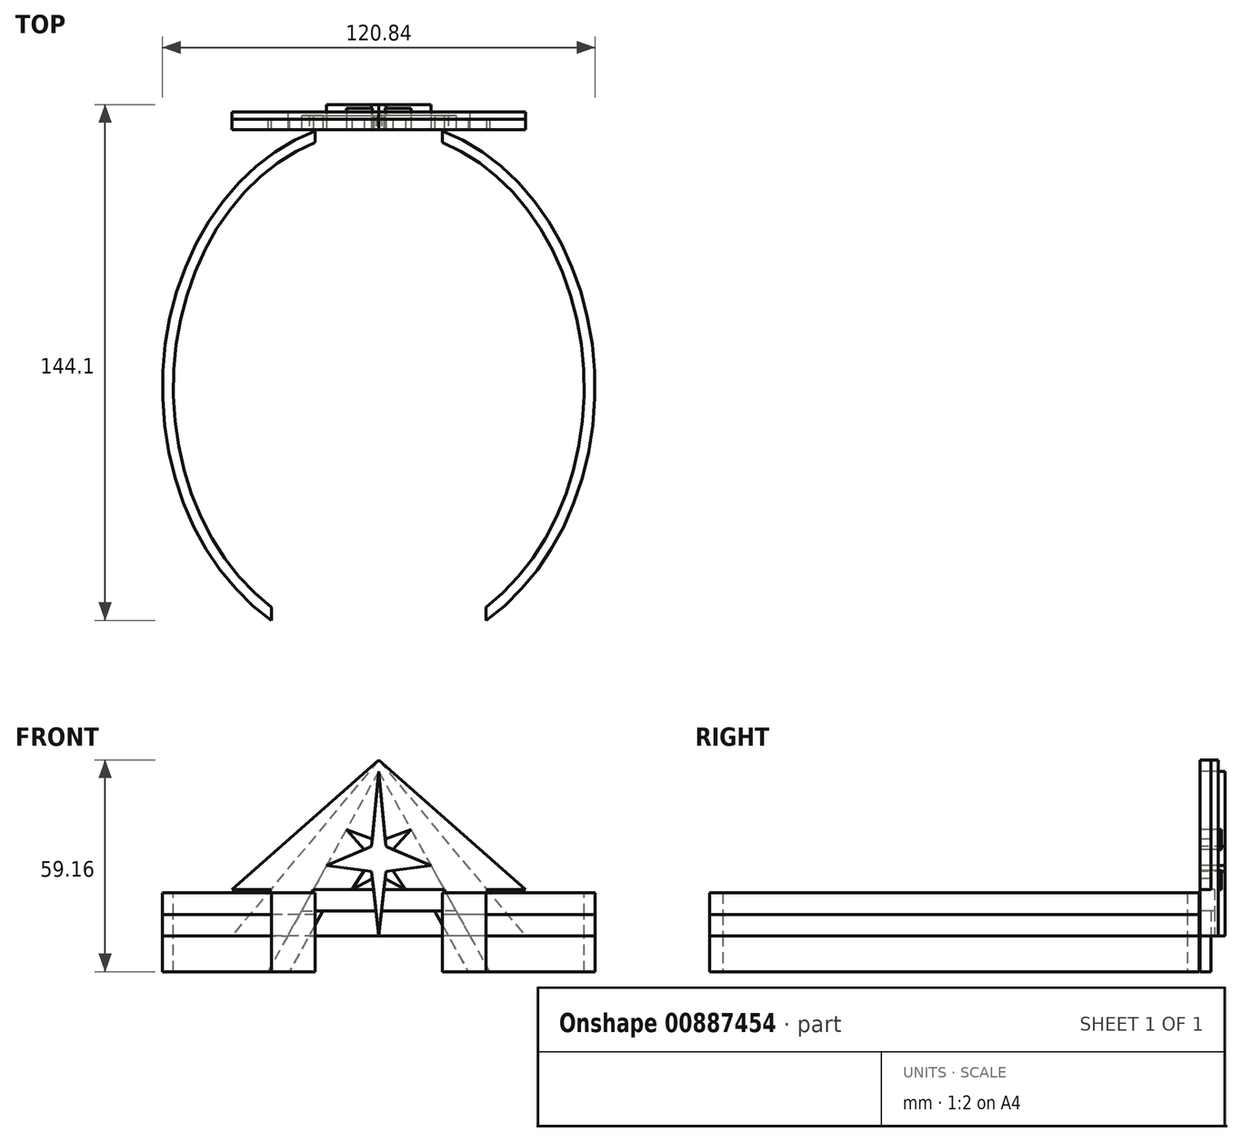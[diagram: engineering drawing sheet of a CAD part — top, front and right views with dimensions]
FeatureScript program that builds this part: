
annotation { "Feature Type Name" : "Feature", "Feature Type Description" : "" }
export const myFeature = defineFeature(function(context is Context, id is Id, definition is map)
    precondition{}
    {
        {
            var Q0;
            Q0=qCreatedBy(makeId("Top.planeOp"),FACE);
            var sketch = newSketch(context, id + "F0", { "sketchPlane" : qUnion([Q0])});
            skEllipse(sketch, "E0", {"center": v(0, 0) * mm, "majorRadius": 75 * mm, "minorRadius": 60.42 * mm, "majorAxis": v(0, 1)});
            skEllipse(sketch, "E1", {"center": v(0, 0) * mm, "majorRadius": 72 * mm, "minorRadius": 57.42 * mm, "majorAxis": v(0, 1)});
            skPoint(sketch, "E2", {"position": v(-60.42, 0) * mm});
            skPoint(sketch, "E3", {"position": v(-57.42, 0) * mm});
            skPoint(sketch, "E4", {"position": v(0, 7.93) * mm});
            skPoint(sketch, "E5", {"position": v(0, 72) * mm});
            skPoint(sketch, "E6", {"position": v(0, 75) * mm});
            skLineSegment(sketch, "E7.bottom", {"start": v(-30, 0) * mm, "end": v(30, 0) * mm});
            skLineSegment(sketch, "E7.top", {"start": v(-30, -85.78) * mm, "end": v(30, -85.78) * mm});
            skLineSegment(sketch, "E7.left", {"start": v(-30, 0) * mm, "end": v(-30, -85.78) * mm});
            skLineSegment(sketch, "E7.right", {"start": v(30, 0) * mm, "end": v(30, -85.78) * mm});
            skPoint(sketch, "E8", {"position": v(30, 0) * mm});
            skPoint(sketch, "E9", {"position": v(30, 74.8) * mm});
            skPoint(sketch, "E10", {"position": v(-30, 0) * mm});
            skPoint(sketch, "E11", {"position": v(-30, 74.8) * mm});
            skLineSegment(sketch, "E12.bottom", {"start": v(17.75, 57.73) * mm, "end": v(-17.75, 57.73) * mm});
            skLineSegment(sketch, "E12.top", {"start": v(17.75, 82.73) * mm, "end": v(-17.75, 82.73) * mm});
            skLineSegment(sketch, "E12.left", {"start": v(17.75, 57.73) * mm, "end": v(17.75, 82.73) * mm});
            skLineSegment(sketch, "E12.right", {"start": v(-17.75, 57.73) * mm, "end": v(-17.75, 82.73) * mm});
            skPoint(sketch, "E13", {"position": v(0, 57.73) * mm});
            skSolve(sketch);
        }
        {
            var Q0;
            {var subQ0=sQuery(id+"F0.wireOp",EDGE,"E7.left");var subQ1=sQuery(id+"F0.wireOp",EDGE,"E0");var subQ2=makeQuery(id+"F0.imprint","INTERSECT",VERTEX,{"derivedFrom":[subQ1,subQ0]});Q0=makeQuery(id+"F0.imprint","IMPRINT",FACE,{"disambiguationData":[TD([[makeQuery(id+"F0.imprint","IMPRINT",EDGE,{"disambiguationData":[TD([[subQ2,1.0]])],"derivedFrom":subQ1}),1.0]])]});}
            var Q1;
            {var subQ0=sQuery(id+"F0.wireOp",EDGE,"E7.right");var subQ1=sQuery(id+"F0.wireOp",EDGE,"E0");var subQ2=makeQuery(id+"F0.imprint","INTERSECT",VERTEX,{"derivedFrom":[subQ1,subQ0]});Q1=makeQuery(id+"F0.imprint","IMPRINT",FACE,{"disambiguationData":[TD([[makeQuery(id+"F0.imprint","IMPRINT",EDGE,{"disambiguationData":[TD([[subQ2,-1.0]])],"derivedFrom":subQ1}),1.0]])]});}
            extrude(context, id + "F1", {"entities" : qUnion([Q0, Q1]), "depth" : 10 * mm, "offsetDistance" : 25 * mm});
        }
        {
            var Q0;
            Q0=qCreatedBy(makeId("Top.planeOp"),FACE);
            cPlane(context, id + "F2", {"entities" : qUnion([Q0]), "cplaneType" : CPlaneType.OFFSET, "offset" : 10 * mm, "width" : 150 * mm, "height" : 150 * mm});
        }
        {
            var Q0;
            Q0=qCreatedBy(makeId("Top.planeOp"),FACE);
            cPlane(context, id + "F3", {"entities" : qUnion([Q0]), "cplaneType" : CPlaneType.OFFSET, "offset" : 16 * mm, "width" : 150 * mm, "height" : 150 * mm});
        }
        {
            var Q0;
            Q0=qCreatedBy(id+"F2.planeOp",FACE);
            var sketch = newSketch(context, id + "F4", { "sketchPlane" : qUnion([Q0])});
            skEllipse(sketch, "E14", {"center": v(0, 0) * mm, "majorRadius": 75 * mm, "minorRadius": 60.42 * mm, "majorAxis": v(0, 1)});
            skEllipse(sketch, "E15", {"center": v(0, 0) * mm, "majorRadius": 72 * mm, "minorRadius": 57.42 * mm, "majorAxis": v(0, 1)});
            skPoint(sketch, "E16", {"position": v(-60.42, 0) * mm});
            skPoint(sketch, "E17", {"position": v(-57.42, 0) * mm});
            skPoint(sketch, "E18", {"position": v(0, -14.53) * mm});
            skPoint(sketch, "E19", {"position": v(0, 72) * mm});
            skPoint(sketch, "E20", {"position": v(0, 75) * mm});
            skLineSegment(sketch, "E21.bottom", {"start": v(-30, 0) * mm, "end": v(30, 0) * mm});
            skLineSegment(sketch, "E21.top", {"start": v(-30, -85.78) * mm, "end": v(30, -85.78) * mm});
            skLineSegment(sketch, "E21.left", {"start": v(-30, 0) * mm, "end": v(-30, -85.78) * mm});
            skLineSegment(sketch, "E21.right", {"start": v(30, 0) * mm, "end": v(30, -85.78) * mm});
            skPoint(sketch, "E22", {"position": v(30, 0) * mm});
            skPoint(sketch, "E23", {"position": v(30, 52.33) * mm});
            skPoint(sketch, "E24", {"position": v(-30, 0) * mm});
            skPoint(sketch, "E25", {"position": v(-30, 52.33) * mm});
            skLineSegment(sketch, "E26.bottom", {"start": v(17.75, 57.73) * mm, "end": v(-17.75, 57.73) * mm});
            skLineSegment(sketch, "E26.top", {"start": v(17.75, 82.73) * mm, "end": v(-17.75, 82.73) * mm});
            skLineSegment(sketch, "E26.left", {"start": v(17.75, 57.73) * mm, "end": v(17.75, 82.73) * mm});
            skLineSegment(sketch, "E26.right", {"start": v(-17.75, 57.73) * mm, "end": v(-17.75, 82.73) * mm});
            skPoint(sketch, "E27", {"position": v(0, 57.73) * mm});
            skSolve(sketch);
        }
        {
            var Q0;
            Q0=qCreatedBy(makeId("Front.planeOp"),FACE);
            cPlane(context, id + "F5", {"entities" : qUnion([Q0]), "cplaneType" : CPlaneType.OFFSET, "offset" : 72 * mm, "oppositeDirection" : true, "width" : 150 * mm, "height" : 150 * mm});
        }
        {
            var Q0;
            Q0=qCreatedBy(id+"F5.planeOp",FACE);
            var sketch = newSketch(context, id + "F6", { "sketchPlane" : qUnion([Q0])});
            skPoint(sketch, "E28", {"position": v(0, 56) * mm});
            skLineSegment(sketch, "E29", {"start": v(0, 56) * mm, "end": v(30.98, 0) * mm});
            skPoint(sketch, "E30", {"position": v(40.98, 0) * mm});
            skPoint(sketch, "E31", {"position": v(40.98, 10) * mm});
            skPoint(sketch, "E32", {"position": v(0, 59.16) * mm});
            skLineSegment(sketch, "E33", {"start": v(0, 59.16) * mm, "end": v(40.98, 10) * mm});
            skPoint(sketch, "E34", {"position": v(40.98, 23) * mm});
            skLineSegment(sketch, "E35", {"start": v(0, 59.16) * mm, "end": v(40.98, 23) * mm});
            skPoint(sketch, "E36", {"position": v(30.15, 23) * mm});
            skPoint(sketch, "E37", {"position": v(40.98, 17) * mm});
            skPoint(sketch, "E38", {"position": v(21.58, 17) * mm});
            skPoint(sketch, "E39", {"position": v(18.26, 23) * mm});
            skLineSegment(sketch, "E40", {"start": v(18.26, 23) * mm, "end": v(0, 23) * mm});
            skLineSegment(sketch, "E41", {"start": v(21.58, 17) * mm, "end": v(0, 17) * mm});
            skPoint(sketch, "E42", {"position": v(0, 17) * mm});
            skPoint(sketch, "E43", {"position": v(0, 10) * mm});
            skPoint(sketch, "E44", {"position": v(24.98, 0) * mm});
            skPoint(sketch, "E45", {"position": v(15.58, 17) * mm});
            skLineSegment(sketch, "E46", {"start": v(15.58, 17) * mm, "end": v(24.98, 0) * mm});
            skPoint(sketch, "E47", {"position": v(25.45, 10) * mm});
            skLineSegment(sketch, "E48", {"start": v(19.45, 10) * mm, "end": v(0, 10) * mm});
            skLineSegment(sketch, "E49", {"start": v(40.98, 23) * mm, "end": v(30.15, 23) * mm});
            skPoint(sketch, "E50", {"position": v(0, 28) * mm});
            skPoint(sketch, "E51", {"position": v(0, 35) * mm});
            skPoint(sketch, "E52", {"position": v(2, 28) * mm});
            skPoint(sketch, "E53", {"position": v(2, 35) * mm});
            skLineSegment(sketch, "E54", {"start": v(0, 56) * mm, "end": v(2, 35) * mm});
            skLineSegment(sketch, "E55", {"start": v(2, 28) * mm, "end": v(2, 35) * mm});
            skLineSegment(sketch, "E56", {"start": v(2, 28) * mm, "end": v(0, 10) * mm});
            skPoint(sketch, "E57", {"position": v(14.56, 29.69) * mm});
            skLineSegment(sketch, "E58", {"start": v(2, 35) * mm, "end": v(14.56, 29.69) * mm});
            skLineSegment(sketch, "E59", {"start": v(2, 28) * mm, "end": v(14.56, 29.69) * mm});
            skPoint(sketch, "E60", {"position": v(9.02, 39.69) * mm});
            skPoint(sketch, "E61", {"position": v(4, 34.15) * mm});
            skPoint(sketch, "E62", {"position": v(1.81, 37) * mm});
            skLineSegment(sketch, "E63", {"start": v(9.02, 39.69) * mm, "end": v(4, 34.15) * mm});
            skLineSegment(sketch, "E64", {"start": v(9.02, 39.69) * mm, "end": v(1.81, 37) * mm});
            skPoint(sketch, "E65", {"position": v(7.44, 23) * mm});
            skPoint(sketch, "E66", {"position": v(1.44, 23) * mm});
            skPoint(sketch, "E67", {"position": v(4, 28.27) * mm});
            skLineSegment(sketch, "E68", {"start": v(4, 28.27) * mm, "end": v(7.44, 23) * mm});
            skPoint(sketch, "E69", {"position": v(1.78, 26) * mm});
            skLineSegment(sketch, "E70", {"start": v(1.78, 26) * mm, "end": v(7.44, 23) * mm});
            skLineSegment(sketch, "E71.MirrorCS", {"start": v(0, 56) * mm, "end": v(-2, 35) * mm});
            skLineSegment(sketch, "E72.MirrorCS", {"start": v(-9.02, 39.69) * mm, "end": v(-1.81, 37) * mm});
            skLineSegment(sketch, "E73.MirrorCS", {"start": v(0, 56) * mm, "end": v(-30.98, 0) * mm});
            skLineSegment(sketch, "E74.MirrorCS", {"start": v(-9.02, 39.69) * mm, "end": v(-4, 34.15) * mm});
            skLineSegment(sketch, "E75.MirrorCS", {"start": v(-2, 35) * mm, "end": v(-14.56, 29.69) * mm});
            skLineSegment(sketch, "E76.MirrorCS", {"start": v(-2, 28) * mm, "end": v(-14.56, 29.69) * mm});
            skLineSegment(sketch, "E77.MirrorCS", {"start": v(-4, 28.27) * mm, "end": v(-7.44, 23) * mm});
            skLineSegment(sketch, "E78.MirrorCS", {"start": v(-1.78, 26) * mm, "end": v(-7.44, 23) * mm});
            skLineSegment(sketch, "E79.MirrorCS", {"start": v(-18.26, 23) * mm, "end": v(0, 23) * mm});
            skLineSegment(sketch, "E80.MirrorCS", {"start": v(-21.58, 17) * mm, "end": v(0, 17) * mm});
            skLineSegment(sketch, "E81.MirrorCS", {"start": v(-15.58, 17) * mm, "end": v(-24.98, 0) * mm});
            skLineSegment(sketch, "E82.MirrorCS", {"start": v(-19.45, 10) * mm, "end": v(0, 10) * mm});
            skLineSegment(sketch, "E83.MirrorCS", {"start": v(-2, 28) * mm, "end": v(0, 10) * mm});
            skLineSegment(sketch, "E84.MirrorCS", {"start": v(0, 59.16) * mm, "end": v(-40.98, 10) * mm});
            skLineSegment(sketch, "E85.MirrorCS", {"start": v(0, 59.16) * mm, "end": v(-40.98, 23) * mm});
            skLineSegment(sketch, "E86.MirrorCS", {"start": v(-40.98, 23) * mm, "end": v(-30.15, 23) * mm});
            skLineSegment(sketch, "E87", {"start": v(40.98, 10) * mm, "end": v(25.45, 10) * mm});
            skLineSegment(sketch, "E88.MirrorCS", {"start": v(-40.98, 10) * mm, "end": v(-25.45, 10) * mm});
            skLineSegment(sketch, "E89", {"start": v(-24.98, 0) * mm, "end": v(-30.98, 0) * mm});
            skLineSegment(sketch, "E90", {"start": v(30.98, 0) * mm, "end": v(24.98, 0) * mm});
            skSolve(sketch);
        }
        {
            var Q0;
            {var subQ0=sQuery(id+"F6.wireOp",EDGE,"E87");Q0=makeQuery(id+"F6.imprint","IMPRINT",FACE,{"disambiguationData":[TD([[makeQuery(id+"F6.imprint","IMPRINT",EDGE,{"derivedFrom":subQ0}),-1.0]])]});}
            extrude(context, id + "F7", {"entities" : qUnion([Q0]), "oppositeDirection" : true, "depth" : 5 * mm, "offsetDistance" : 25 * mm});
        }
        {
            var Q0;
            {var subQ0=sQuery(id+"F6.wireOp",EDGE,"E35");Q0=makeQuery(id+"F6.imprint","IMPRINT",FACE,{"disambiguationData":[TD([[makeQuery(id+"F6.imprint","IMPRINT",EDGE,{"derivedFrom":subQ0}),-1.0]])]});}
            var Q1;
            {var subQ0=sQuery(id+"F6.wireOp",EDGE,"E85.MirrorCS");Q1=makeQuery(id+"F6.imprint","IMPRINT",FACE,{"disambiguationData":[TD([[makeQuery(id+"F6.imprint","IMPRINT",EDGE,{"derivedFrom":subQ0}),1.0]])]});}
            var Q2;
            {var subQ5=sQuery(id+"F6.wireOp",EDGE,"E68");Q2=makeQuery(id+"F6.imprint","IMPRINT",FACE,{"disambiguationData":[TD([[makeQuery(id+"F6.imprint","IMPRINT",EDGE,{"derivedFrom":subQ5}),1.0]])]});}
            var Q3;
            {var subQ3=sQuery(id+"F6.wireOp",EDGE,"E63");Q3=makeQuery(id+"F6.imprint","IMPRINT",FACE,{"disambiguationData":[TD([[makeQuery(id+"F6.imprint","IMPRINT",EDGE,{"derivedFrom":subQ3}),1.0]])]});}
            var Q4;
            {var subQ3=sQuery(id+"F6.wireOp",EDGE,"E64");Q4=makeQuery(id+"F6.imprint","IMPRINT",FACE,{"disambiguationData":[TD([[makeQuery(id+"F6.imprint","IMPRINT",EDGE,{"derivedFrom":subQ3}),-1.0]])]});}
            var Q5;
            {var subQ3=sQuery(id+"F6.wireOp",EDGE,"E72.MirrorCS");Q5=makeQuery(id+"F6.imprint","IMPRINT",FACE,{"disambiguationData":[TD([[makeQuery(id+"F6.imprint","IMPRINT",EDGE,{"derivedFrom":subQ3}),1.0]])]});}
            var Q6;
            {var subQ0=sQuery(id+"F6.wireOp",EDGE,"E74.MirrorCS");Q6=makeQuery(id+"F6.imprint","IMPRINT",FACE,{"disambiguationData":[TD([[makeQuery(id+"F6.imprint","IMPRINT",EDGE,{"derivedFrom":subQ0}),-1.0]])]});}
            var Q7;
            {var subQ3=sQuery(id+"F6.wireOp",EDGE,"E77.MirrorCS");Q7=makeQuery(id+"F6.imprint","IMPRINT",FACE,{"disambiguationData":[TD([[makeQuery(id+"F6.imprint","IMPRINT",EDGE,{"derivedFrom":subQ3}),-1.0]])]});}
            var Q8;
            {var subQ7=sQuery(id+"F6.wireOp",EDGE,"E90");Q8=makeQuery(id+"F6.imprint","IMPRINT",FACE,{"disambiguationData":[TD([[makeQuery(id+"F6.imprint","IMPRINT",EDGE,{"derivedFrom":subQ7}),-1.0]])]});}
            var Q9;
            {var subQ5=sQuery(id+"F6.wireOp",EDGE,"E89");Q9=makeQuery(id+"F6.imprint","IMPRINT",FACE,{"disambiguationData":[TD([[makeQuery(id+"F6.imprint","IMPRINT",EDGE,{"derivedFrom":subQ5}),-1.0]])]});}
            var Q10;
            {var subQ0=sQuery(id+"F6.wireOp",EDGE,"E70");Q10=makeQuery(id+"F6.imprint","IMPRINT",FACE,{"disambiguationData":[TD([[makeQuery(id+"F6.imprint","IMPRINT",EDGE,{"derivedFrom":subQ0}),-1.0]])]});}
            var Q11;
            {var subQ0=sQuery(id+"F6.wireOp",EDGE,"E78.MirrorCS");Q11=makeQuery(id+"F6.imprint","IMPRINT",FACE,{"disambiguationData":[TD([[makeQuery(id+"F6.imprint","IMPRINT",EDGE,{"derivedFrom":subQ0}),1.0]])]});}
            extrude(context, id + "F8", {"entities" : qUnion([Q0, Q1, Q2, Q3, Q4, Q5, Q6, Q7, Q8, Q9, Q10, Q11]), "operationType" : NewBodyOperationType.ADD, "oppositeDirection" : true, "depth" : 3 * mm, "offsetDistance" : 25 * mm});
        }
        {
            var Q0;
            {var subQ1=sQuery(id+"F6.wireOp",EDGE,"E29");var subQ5=sQuery(id+"F6.wireOp",EDGE,"E40");var subQ9=makeQuery(id+"F6.imprint","INTERSECT",VERTEX,{"derivedFrom":[subQ1,subQ5]});Q0=makeQuery(id+"F6.imprint","IMPRINT",FACE,{"disambiguationData":[TD([[makeQuery(id+"F6.imprint","IMPRINT",EDGE,{"disambiguationData":[TD([[subQ9,-1.0]])],"derivedFrom":subQ1}),-1.0]])]});}
            var Q1;
            {var subQ1=sQuery(id+"F6.wireOp",EDGE,"E73.MirrorCS");var subQ4=sQuery(id+"F6.wireOp",EDGE,"E79.MirrorCS");var subQ5=makeQuery(id+"F6.imprint","INTERSECT",VERTEX,{"derivedFrom":[subQ4,subQ1]});Q1=makeQuery(id+"F6.imprint","IMPRINT",FACE,{"disambiguationData":[TD([[makeQuery(id+"F6.imprint","IMPRINT",EDGE,{"disambiguationData":[TD([[subQ5,-1.0]])],"derivedFrom":subQ1}),1.0]])]});}
            extrude(context, id + "F9", {"entities" : qUnion([Q0, Q1]), "oppositeDirection" : true, "depth" : 4 * mm, "offsetDistance" : 25 * mm});
        }
        {
            var Q0;
            {var subQ16=sQuery(id+"F6.wireOp",EDGE,"E55");Q0=makeQuery(id+"F6.imprint","IMPRINT",FACE,{"disambiguationData":[TD([[makeQuery(id+"F6.imprint","IMPRINT",EDGE,{"derivedFrom":subQ16}),1.0]])]});}
            var Q1;
            {var subQ1=sQuery(id+"F6.wireOp",EDGE,"E55");Q1=makeQuery(id+"F6.imprint","IMPRINT",FACE,{"disambiguationData":[TD([[makeQuery(id+"F6.imprint","IMPRINT",EDGE,{"derivedFrom":subQ1}),-1.0]])]});}
            var Q2;
            {var subQ0=sQuery(id+"F6.wireOp",EDGE,"E79.MirrorCS");var subQ1=sQuery(id+"F6.wireOp",EDGE,"E40");var subQ2=makeQuery(id+"F6.imprint","INTERSECT",VERTEX,{"derivedFrom":[subQ1,subQ0]});Q2=makeQuery(id+"F6.imprint","IMPRINT",FACE,{"disambiguationData":[TD([[makeQuery(id+"F6.imprint","IMPRINT",EDGE,{"disambiguationData":[TD([[subQ2,1.0]])],"derivedFrom":subQ1}),1.0]])]});}
            var Q3;
            {var subQ0=sQuery(id+"F6.wireOp",EDGE,"E80.MirrorCS");var subQ1=sQuery(id+"F6.wireOp",EDGE,"E41");var subQ2=makeQuery(id+"F6.imprint","INTERSECT",VERTEX,{"derivedFrom":[subQ1,subQ0]});Q3=makeQuery(id+"F6.imprint","IMPRINT",FACE,{"disambiguationData":[TD([[makeQuery(id+"F6.imprint","IMPRINT",EDGE,{"disambiguationData":[TD([[subQ2,1.0]])],"derivedFrom":subQ1}),1.0]])]});}
            extrude(context, id + "F10", {"entities" : qUnion([Q0, Q1, Q2, Q3]), "oppositeDirection" : true, "depth" : 7 * mm, "offsetDistance" : 25 * mm});
        }
        {
            var Q0;
            {var subQ4=sQuery(id+"F6.wireOp",EDGE,"E63");Q0=makeQuery(id+"F6.imprint","IMPRINT",FACE,{"disambiguationData":[TD([[makeQuery(id+"F6.imprint","IMPRINT",EDGE,{"derivedFrom":subQ4}),-1.0]])]});}
            var Q1;
            {var subQ4=sQuery(id+"F6.wireOp",EDGE,"E68");Q1=makeQuery(id+"F6.imprint","IMPRINT",FACE,{"disambiguationData":[TD([[makeQuery(id+"F6.imprint","IMPRINT",EDGE,{"derivedFrom":subQ4}),-1.0]])]});}
            var Q2;
            {var subQ3=sQuery(id+"F6.wireOp",EDGE,"E77.MirrorCS");Q2=makeQuery(id+"F6.imprint","IMPRINT",FACE,{"disambiguationData":[TD([[makeQuery(id+"F6.imprint","IMPRINT",EDGE,{"derivedFrom":subQ3}),1.0]])]});}
            var Q3;
            {var subQ3=sQuery(id+"F6.wireOp",EDGE,"E72.MirrorCS");Q3=makeQuery(id+"F6.imprint","IMPRINT",FACE,{"disambiguationData":[TD([[makeQuery(id+"F6.imprint","IMPRINT",EDGE,{"derivedFrom":subQ3}),-1.0]])]});}
            extrude(context, id + "F11", {"entities" : qUnion([Q0, Q1, Q2, Q3]), "oppositeDirection" : true, "depth" : 6 * mm, "offsetDistance" : 25 * mm});
        }
        {
            var Q0;
            {var subQ5=sQuery(id+"F6.wireOp",EDGE,"E48");Q0=makeQuery(id+"F6.imprint","IMPRINT",FACE,{"disambiguationData":[TD([[makeQuery(id+"F6.imprint","IMPRINT",EDGE,{"derivedFrom":subQ5}),-1.0]])]});}
            var Q1;
            {var subQ5=sQuery(id+"F6.wireOp",EDGE,"E82.MirrorCS");Q1=makeQuery(id+"F6.imprint","IMPRINT",FACE,{"disambiguationData":[TD([[makeQuery(id+"F6.imprint","IMPRINT",EDGE,{"derivedFrom":subQ5}),1.0]])]});}
            extrude(context, id + "F12", {"entities" : qUnion([Q0, Q1]), "oppositeDirection" : true, "depth" : 4 * mm, "offsetDistance" : 25 * mm});
        }
        {
            var Q0;
            {var subQ0=sQuery(id+"F4.wireOp",EDGE,"E21.right");var subQ1=sQuery(id+"F4.wireOp",EDGE,"E14");var subQ2=makeQuery(id+"F4.imprint","INTERSECT",VERTEX,{"derivedFrom":[subQ1,subQ0]});Q0=makeQuery(id+"F4.imprint","IMPRINT",FACE,{"disambiguationData":[TD([[makeQuery(id+"F4.imprint","IMPRINT",EDGE,{"disambiguationData":[TD([[subQ2,-1.0]])],"derivedFrom":subQ1}),1.0]])]});}
            var Q1;
            {var subQ0=sQuery(id+"F4.wireOp",EDGE,"E21.left");var subQ1=sQuery(id+"F4.wireOp",EDGE,"E14");var subQ2=makeQuery(id+"F4.imprint","INTERSECT",VERTEX,{"derivedFrom":[subQ1,subQ0]});Q1=makeQuery(id+"F4.imprint","IMPRINT",FACE,{"disambiguationData":[TD([[makeQuery(id+"F4.imprint","IMPRINT",EDGE,{"disambiguationData":[TD([[subQ2,1.0]])],"derivedFrom":subQ1}),1.0]])]});}
            extrude(context, id + "F13", {"entities" : qUnion([Q0, Q1]), "depth" : 6 * mm, "offsetDistance" : 25 * mm});
        }
        {
            var Q0;
            Q0=qCreatedBy(id+"F3.planeOp",FACE);
            var sketch = newSketch(context, id + "F14", { "sketchPlane" : qUnion([Q0])});
            skEllipse(sketch, "E91", {"center": v(0, 0) * mm, "majorRadius": 75 * mm, "minorRadius": 60.42 * mm, "majorAxis": v(0, 1)});
            skEllipse(sketch, "E92", {"center": v(0, 0) * mm, "majorRadius": 72 * mm, "minorRadius": 57.42 * mm, "majorAxis": v(0, 1)});
            skPoint(sketch, "E93", {"position": v(-60.42, 0) * mm});
            skPoint(sketch, "E94", {"position": v(-57.42, 0) * mm});
            skPoint(sketch, "E95", {"position": v(0, -14.53) * mm});
            skPoint(sketch, "E96", {"position": v(0, 72) * mm});
            skPoint(sketch, "E97", {"position": v(0, 75) * mm});
            skLineSegment(sketch, "E98.bottom", {"start": v(-30, 0) * mm, "end": v(30, 0) * mm});
            skLineSegment(sketch, "E98.top", {"start": v(-30, -85.78) * mm, "end": v(30, -85.78) * mm});
            skLineSegment(sketch, "E98.left", {"start": v(-30, 0) * mm, "end": v(-30, -85.78) * mm});
            skLineSegment(sketch, "E98.right", {"start": v(30, 0) * mm, "end": v(30, -85.78) * mm});
            skPoint(sketch, "E99", {"position": v(30, 0) * mm});
            skPoint(sketch, "E100", {"position": v(30, 52.33) * mm});
            skPoint(sketch, "E101", {"position": v(-30, 0) * mm});
            skPoint(sketch, "E102", {"position": v(-30, 52.33) * mm});
            skLineSegment(sketch, "E103.bottom", {"start": v(17.75, 57.73) * mm, "end": v(-17.75, 57.73) * mm});
            skLineSegment(sketch, "E103.top", {"start": v(17.75, 82.73) * mm, "end": v(-17.75, 82.73) * mm});
            skLineSegment(sketch, "E103.left", {"start": v(17.75, 57.73) * mm, "end": v(17.75, 82.73) * mm});
            skLineSegment(sketch, "E103.right", {"start": v(-17.75, 57.73) * mm, "end": v(-17.75, 82.73) * mm});
            skPoint(sketch, "E104", {"position": v(0, 57.73) * mm});
            skSolve(sketch);
        }
        {
            var Q0;
            {var subQ0=sQuery(id+"F14.wireOp",EDGE,"E98.left");var subQ1=sQuery(id+"F14.wireOp",EDGE,"E91");var subQ2=makeQuery(id+"F14.imprint","INTERSECT",VERTEX,{"derivedFrom":[subQ1,subQ0]});Q0=makeQuery(id+"F14.imprint","IMPRINT",FACE,{"disambiguationData":[TD([[makeQuery(id+"F14.imprint","IMPRINT",EDGE,{"disambiguationData":[TD([[subQ2,1.0]])],"derivedFrom":subQ1}),1.0]])]});}
            var Q1;
            {var subQ0=sQuery(id+"F14.wireOp",EDGE,"E98.right");var subQ1=sQuery(id+"F14.wireOp",EDGE,"E91");var subQ2=makeQuery(id+"F14.imprint","INTERSECT",VERTEX,{"derivedFrom":[subQ1,subQ0]});Q1=makeQuery(id+"F14.imprint","IMPRINT",FACE,{"disambiguationData":[TD([[makeQuery(id+"F14.imprint","IMPRINT",EDGE,{"disambiguationData":[TD([[subQ2,-1.0]])],"derivedFrom":subQ1}),1.0]])]});}
            extrude(context, id + "F15", {"entities" : qUnion([Q0, Q1]), "depth" : 6 * mm, "offsetDistance" : 25 * mm});
        }
    });
